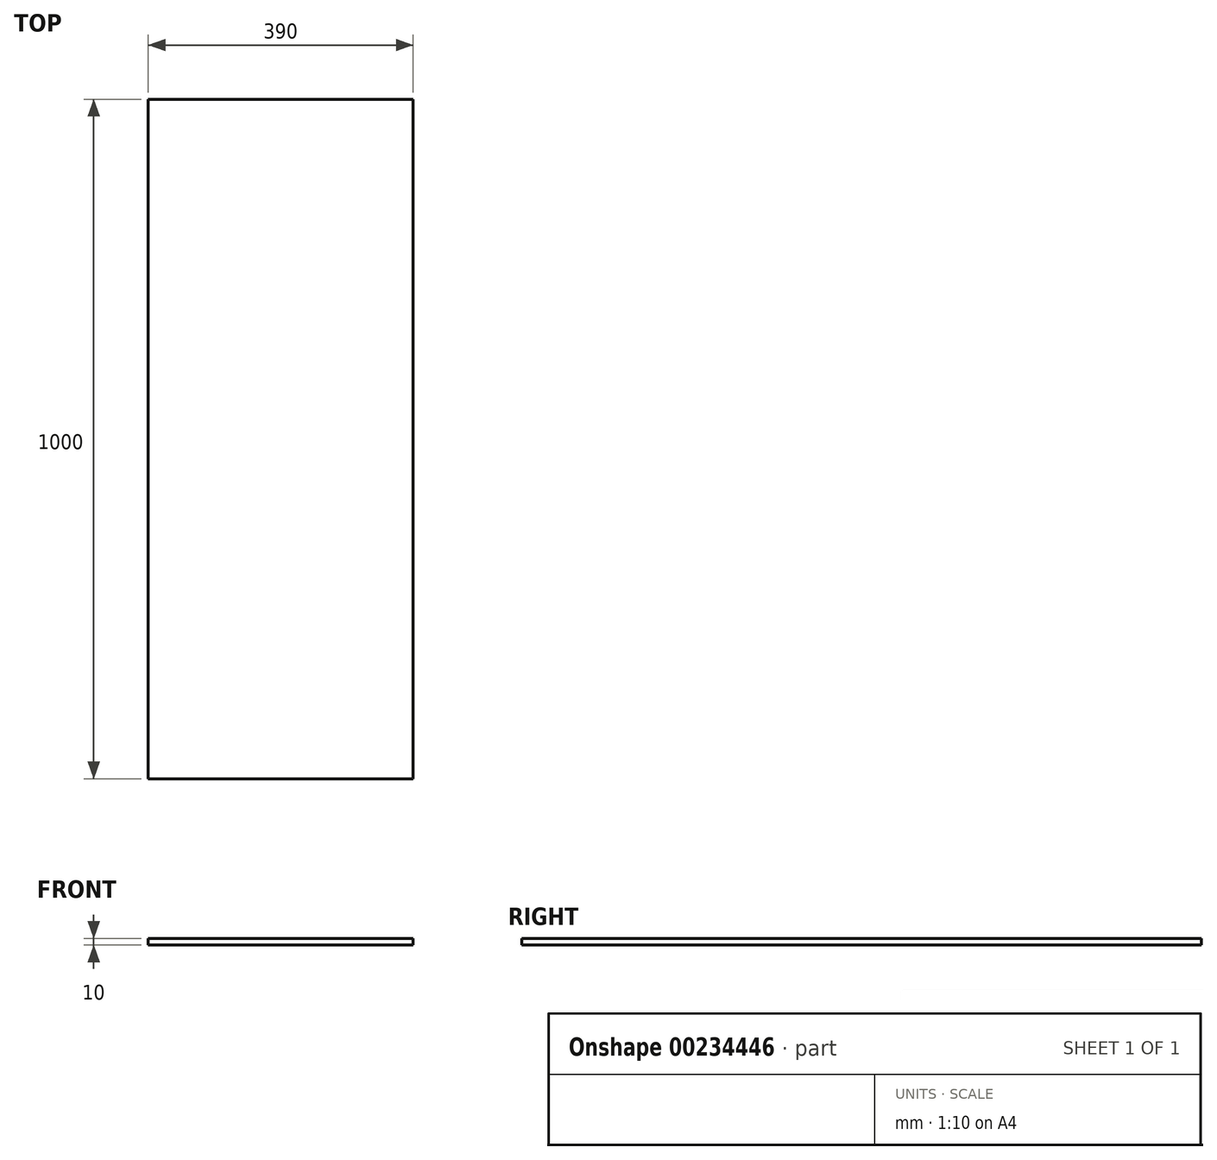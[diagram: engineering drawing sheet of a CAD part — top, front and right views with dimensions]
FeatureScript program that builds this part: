
annotation { "Feature Type Name" : "Feature", "Feature Type Description" : "" }
export const myFeature = defineFeature(function(context is Context, id is Id, definition is map)
    precondition{}
    {
        {
            var Q0;
            Q0=qCreatedBy(makeId("Top.planeOp"),FACE);
            var sketch = newSketch(context, id + "F0", { "sketchPlane" : qUnion([Q0])});
            skLineSegment(sketch, "E0.bottom", {"start": v(195, 500) * mm, "end": v(-195, 500) * mm});
            skLineSegment(sketch, "E0.top", {"start": v(195, -500) * mm, "end": v(-195, -500) * mm});
            skLineSegment(sketch, "E0.left", {"start": v(195, 500) * mm, "end": v(195, -500) * mm});
            skLineSegment(sketch, "E0.right", {"start": v(-195, 500) * mm, "end": v(-195, -500) * mm});
            skPoint(sketch, "E0.middle", {"position": v(0, 0) * mm});
            skSolve(sketch);
        }
        {
            var Q0;
            Q0 = qSketchRegion(id + "F0", true);
            extrude(context, id + "F1", {"entities" : qUnion([Q0]), "depth" : 10 * mm});
        }
    });
